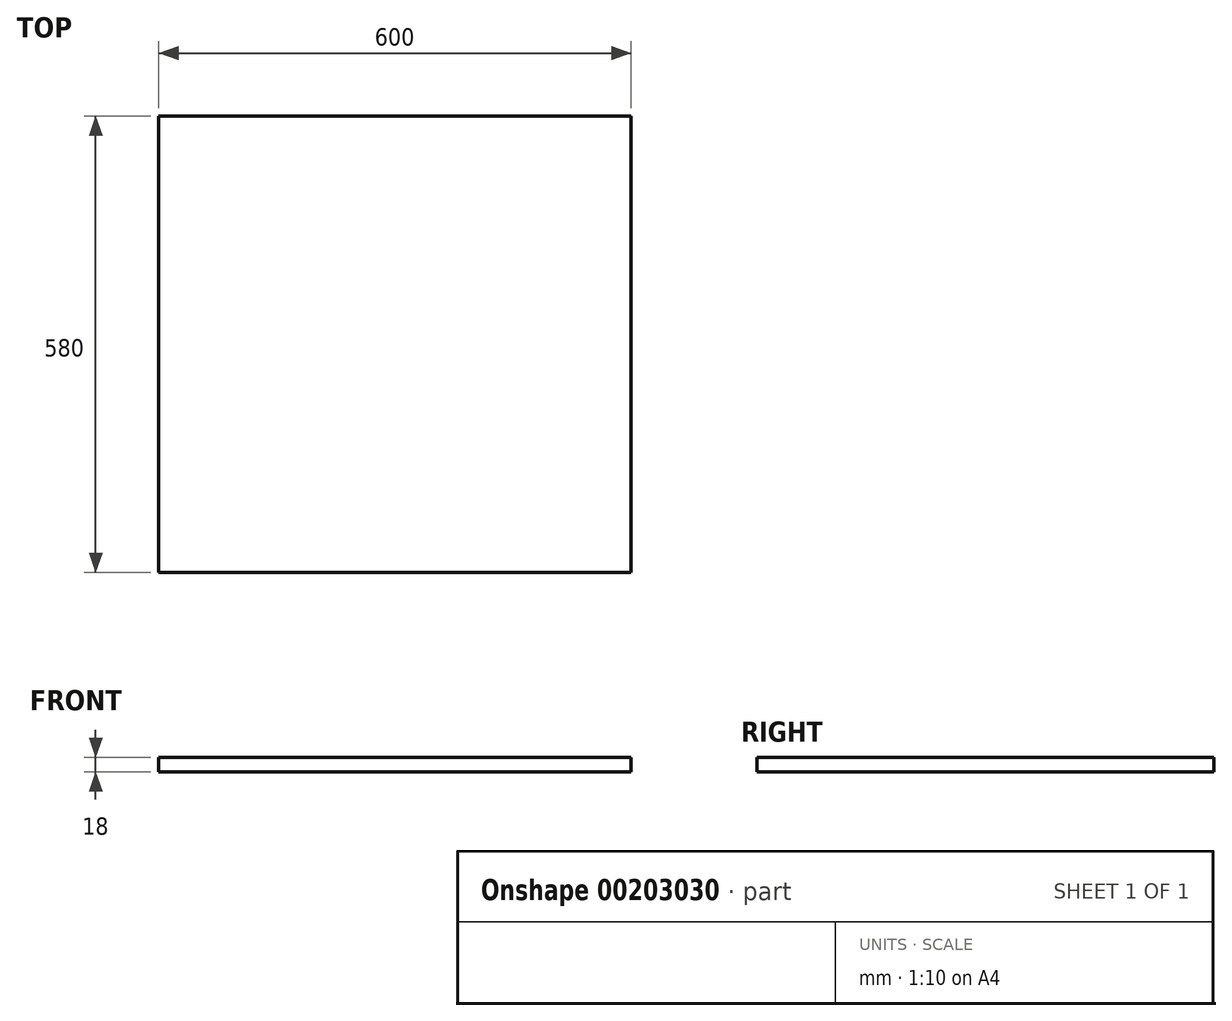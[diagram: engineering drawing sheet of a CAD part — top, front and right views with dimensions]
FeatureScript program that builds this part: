
annotation { "Feature Type Name" : "Feature", "Feature Type Description" : "" }
export const myFeature = defineFeature(function(context is Context, id is Id, definition is map)
    precondition{}
    {
        {
            var Q0;
            Q0=qCreatedBy(makeId("Top.planeOp"),FACE);
            var sketch = newSketch(context, id + "F0", { "sketchPlane" : qUnion([Q0])});
            skLineSegment(sketch, "E0.bottom", {"start": v(-300, -290) * mm, "end": v(300, -290) * mm});
            skLineSegment(sketch, "E0.top", {"start": v(-300, 290) * mm, "end": v(300, 290) * mm});
            skLineSegment(sketch, "E0.left", {"start": v(-300, -290) * mm, "end": v(-300, 290) * mm});
            skLineSegment(sketch, "E0.right", {"start": v(300, -290) * mm, "end": v(300, 290) * mm});
            skPoint(sketch, "E0.middle", {"position": v(0, 0) * mm});
            skSolve(sketch);
        }
        {
            var Q0;
            Q0=makeQuery(id+"F0.imprint","IMPRINT",FACE,{"disambiguationData":[TD([[makeQuery(id+"F0.imprint","IMPRINT",EDGE,{"derivedFrom":sQuery(id+"F0.wireOp",EDGE,"E0.bottom")}),1.0]])]});
            extrude(context, id + "F1", {"entities" : qUnion([Q0]), "depth" : 18 * mm});
        }
    });
